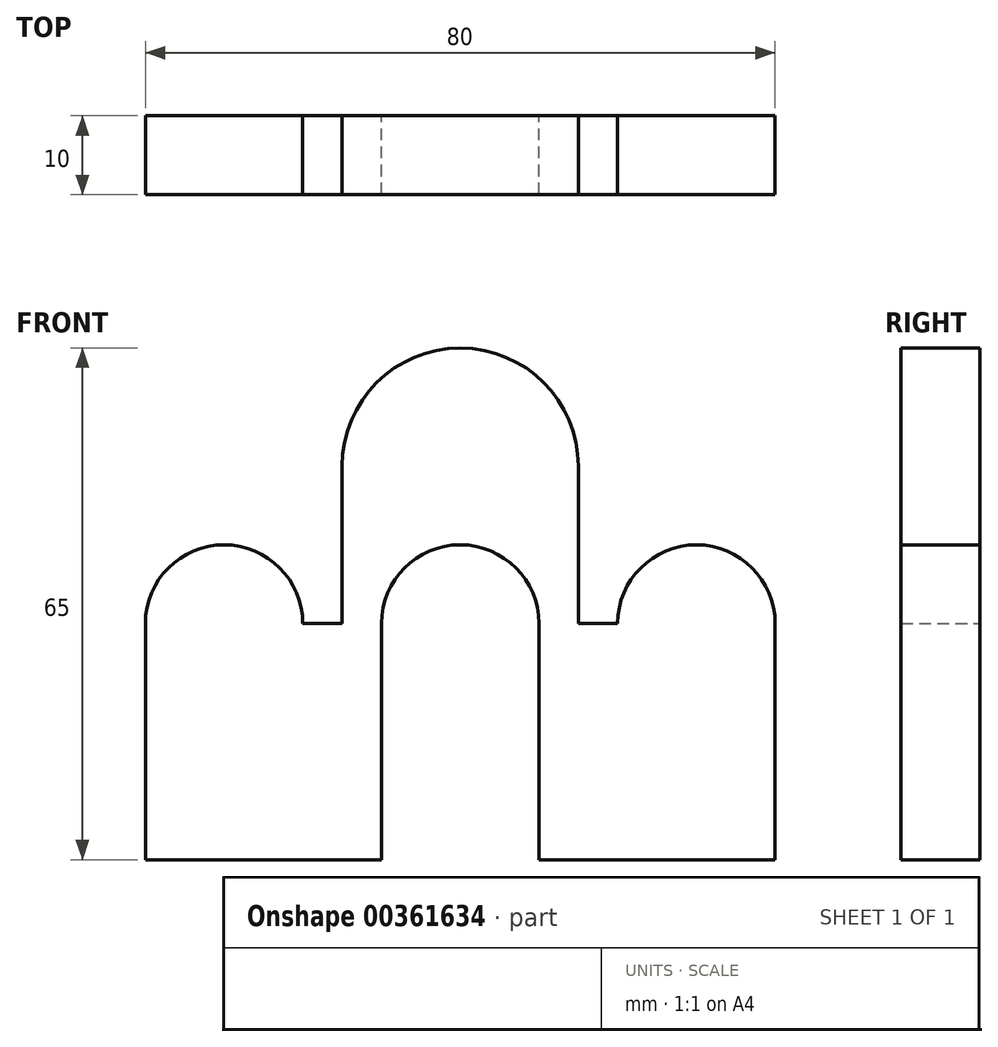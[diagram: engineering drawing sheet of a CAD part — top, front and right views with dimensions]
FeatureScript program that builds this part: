
annotation { "Feature Type Name" : "Feature", "Feature Type Description" : "" }
export const myFeature = defineFeature(function(context is Context, id is Id, definition is map)
    precondition{}
    {
        {
            var Q0;
            Q0=qCreatedBy(makeId("Front.planeOp"),FACE);
            var sketch = newSketch(context, id + "F0", { "sketchPlane" : qUnion([Q0])});
            skLineSegment(sketch, "E0", {"start": v(0, 0) * mm, "end": v(30, 0) * mm});
            skLineSegment(sketch, "E1", {"start": v(30, 0) * mm, "end": v(30, 30) * mm});
            skLineSegment(sketch, "E2", {"start": v(0, 0) * mm, "end": v(0, 30) * mm});
            skArc(sketch, "E3", {"start": v(0, 30) * mm, "mid": v(10, 40) * mm, "end": v(20, 30) * mm});
            skLineSegment(sketch, "E4", {"start": v(0, 30) * mm, "end": v(20, 30) * mm, "construction": true});
            skArc(sketch, "E5", {"start": v(30, 30) * mm, "mid": v(32.93, 37.07) * mm, "end": v(40, 40) * mm});
            skLineSegment(sketch, "E6", {"start": v(40, 30) * mm, "end": v(40, 45.75) * mm, "construction": true});
            skLineSegment(sketch, "E7", {"start": v(20, 30) * mm, "end": v(25, 30) * mm});
            skLineSegment(sketch, "E8", {"start": v(25, 30) * mm, "end": v(25, 50) * mm});
            skArc(sketch, "E9", {"start": v(25, 50) * mm, "mid": v(29.4, 60.6) * mm, "end": v(40, 65) * mm});
            skArc(sketch, "E10.MirrorCS", {"start": v(55, 50) * mm, "mid": v(50.6, 60.6) * mm, "end": v(40, 65) * mm});
            skLineSegment(sketch, "E11.MirrorCS", {"start": v(55, 30) * mm, "end": v(55, 50) * mm});
            skLineSegment(sketch, "E12.MirrorCS", {"start": v(80, 30) * mm, "end": v(60, 30) * mm, "construction": true});
            skArc(sketch, "E13.MirrorCS", {"start": v(80, 30) * mm, "mid": v(70, 40) * mm, "end": v(60, 30) * mm});
            skLineSegment(sketch, "E14.MirrorCS", {"start": v(60, 30) * mm, "end": v(55, 30) * mm});
            skLineSegment(sketch, "E15.MirrorCS", {"start": v(80, 0) * mm, "end": v(80, 30) * mm});
            skLineSegment(sketch, "E16.MirrorCS", {"start": v(50, 0) * mm, "end": v(50, 30) * mm});
            skLineSegment(sketch, "E17.MirrorCS", {"start": v(80, 0) * mm, "end": v(50, 0) * mm});
            skArc(sketch, "E18.MirrorCS", {"start": v(50, 30) * mm, "mid": v(47.07, 37.07) * mm, "end": v(40, 40) * mm});
            skSolve(sketch);
        }
        {
            var Q0;
            Q0=makeQuery(id+"F0.imprint","IMPRINT",FACE,{"disambiguationData":[TD([[makeQuery(id+"F0.imprint","IMPRINT",EDGE,{"derivedFrom":sQuery(id+"F0.wireOp",EDGE,"E0")}),1.0]])]});
            extrude(context, id + "F1", {"entities" : qUnion([Q0]), "depth" : 10 * mm});
        }
    });
